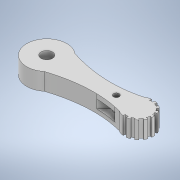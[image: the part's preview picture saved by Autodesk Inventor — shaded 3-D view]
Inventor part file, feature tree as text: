
AUTODESK INVENTOR PART (.ipt)
format: ipt  version: 2020.3 (Build 243373000, 373)  size: 194,048 bytes
history: native  units: mm
features: extrude x4, sketch x4, projected_geometry x1
ambient origin geometry x8: Origin, YZ Plane, XZ Plane, XY Plane, X Axis, Y Axis, Z Axis, Center Point
bodies: Solid1 (feature_tree)
feature tree (9):
  extrude  "Extrusion1"  Depth=3.0mm TaperAngle=0.0deg
  extrude  "Extrusion2"  Depth=80.0mm TaperAngle=180.0deg
  extrude  "Extrusion3"  TaperAngle=135.0deg  [1 undecoded]
  extrude  "Extrusion4"  Depth=0.8mm TaperAngle=0.0deg
  sketch  "Sketch1"  dims[d0=7.0mm d1=5.0mm d2=1.0mm d3=3.0mm d4=0.0mm]
  sketch  "Sketch2"  dims[d5=2.0mm d6=80.0mm d8=180.0deg]
  sketch  "Sketch3"  dims[d10=10.0mm d11=0.0mm d13=135.0deg]
  sketch  "Sketch4"  dims[d14=2.3mm d15=0.0mm d16=0.8mm d17=0.0mm]
  projected_geometry  "Projected Loop1"
note: 1 required parameter value undecoded (feature->parameter linkage not recoverable at this tier; creation-order binding heuristic only, values carry confidence <= 0.55)
